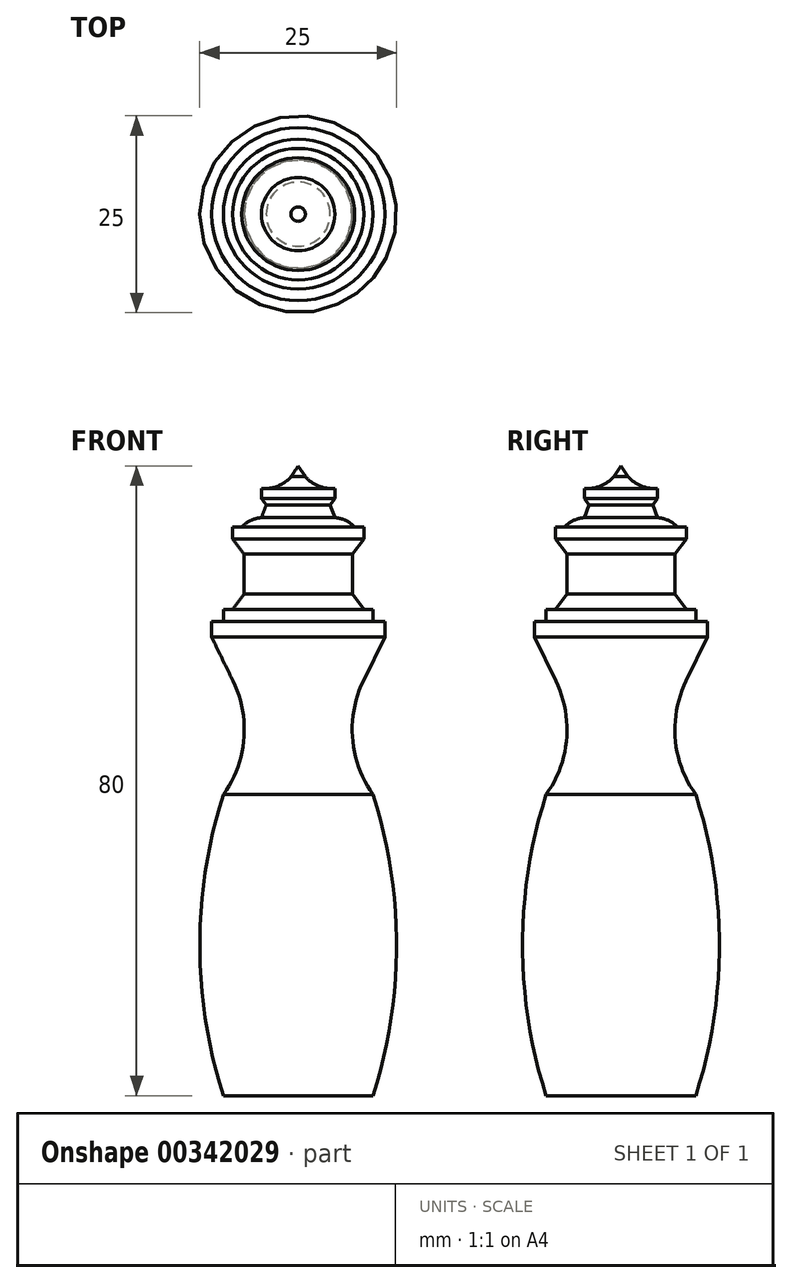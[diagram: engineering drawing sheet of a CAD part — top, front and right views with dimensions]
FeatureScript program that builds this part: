
annotation { "Feature Type Name" : "Feature", "Feature Type Description" : "" }
export const myFeature = defineFeature(function(context is Context, id is Id, definition is map)
    precondition{}
    {
        {
            var Q0;
            Q0=qCreatedBy(makeId("Front.planeOp"),FACE);
            var sketch = newSketch(context, id + "F0", { "sketchPlane" : qUnion([Q0])});
            skLineSegment(sketch, "E0", {"start": v(4.65, -2.86) * mm, "end": v(4.65, -4.14) * mm});
            skLineSegment(sketch, "E1", {"start": v(4.65, -4.14) * mm, "end": v(4.06, -4.93) * mm});
            skLineSegment(sketch, "E2", {"start": v(4.06, -4.93) * mm, "end": v(4.65, -6.55) * mm});
            skArc(sketch, "E3", {"start": v(7.17, -7.75) * mm, "mid": v(6.02, -6.91) * mm, "end": v(4.65, -6.55) * mm});
            skLineSegment(sketch, "E4", {"start": v(7.17, -7.75) * mm, "end": v(8.35, -7.75) * mm});
            skLineSegment(sketch, "E5", {"start": v(8.35, -18.22) * mm, "end": v(9.5, -18.22) * mm});
            skLineSegment(sketch, "E6", {"start": v(9.5, -18.22) * mm, "end": v(9.5, -19.72) * mm});
            skLineSegment(sketch, "E7", {"start": v(9.5, -19.72) * mm, "end": v(11, -19.72) * mm});
            skLineSegment(sketch, "E8", {"start": v(11, -19.72) * mm, "end": v(11, -21.72) * mm});
            skLineSegment(sketch, "E9", {"start": v(0, -80) * mm, "end": v(0, 0) * mm});
            skLineSegment(sketch, "E10", {"start": v(8.35, -7.75) * mm, "end": v(8.35, -9.25) * mm});
            skLineSegment(sketch, "E11", {"start": v(11, -21.72) * mm, "end": v(8.28, -27.3) * mm});
            skArc(sketch, "E12", {"start": v(9.5, -80) * mm, "mid": v(12.5, -60.86) * mm, "end": v(9.5, -41.72) * mm});
            skLineSegment(sketch, "E13", {"start": v(9.5, -80) * mm, "end": v(0, -80) * mm});
            skArc(sketch, "E14", {"start": v(8.28, -27.3) * mm, "mid": v(6.9, -34.68) * mm, "end": v(9.5, -41.72) * mm});
            skLineSegment(sketch, "E15", {"start": v(8.35, -9.25) * mm, "end": v(6.88, -11.2) * mm});
            skLineSegment(sketch, "E16", {"start": v(6.88, -11.2) * mm, "end": v(6.88, -16.27) * mm});
            skLineSegment(sketch, "E17", {"start": v(6.88, -16.27) * mm, "end": v(8.35, -18.22) * mm});
            skLineSegment(sketch, "E18", {"start": v(0, 0) * mm, "end": v(0.92, -1.36) * mm});
            skArc(sketch, "E19", {"start": v(0.92, -1.36) * mm, "mid": v(2.6, -2.55) * mm, "end": v(4.65, -2.86) * mm});
            skSolve(sketch);
        }
        {
            var Q0;
            Q0=makeQuery(id+"F0.imprint","IMPRINT",FACE,{"disambiguationData":[TD([[makeQuery(id+"F0.imprint","IMPRINT",EDGE,{"derivedFrom":sQuery(id+"F0.wireOp",EDGE,"E0")}),-1.0]])]});
            var Q1;
            Q1=sQuery(id+"F0.wireOp",EDGE,"E9");
            revolve(context, id + "F1", {"entities" : qUnion([Q0]), "axis" : qUnion([Q1]), "revolveType" : RevolveType.FULL});
        }
    });
